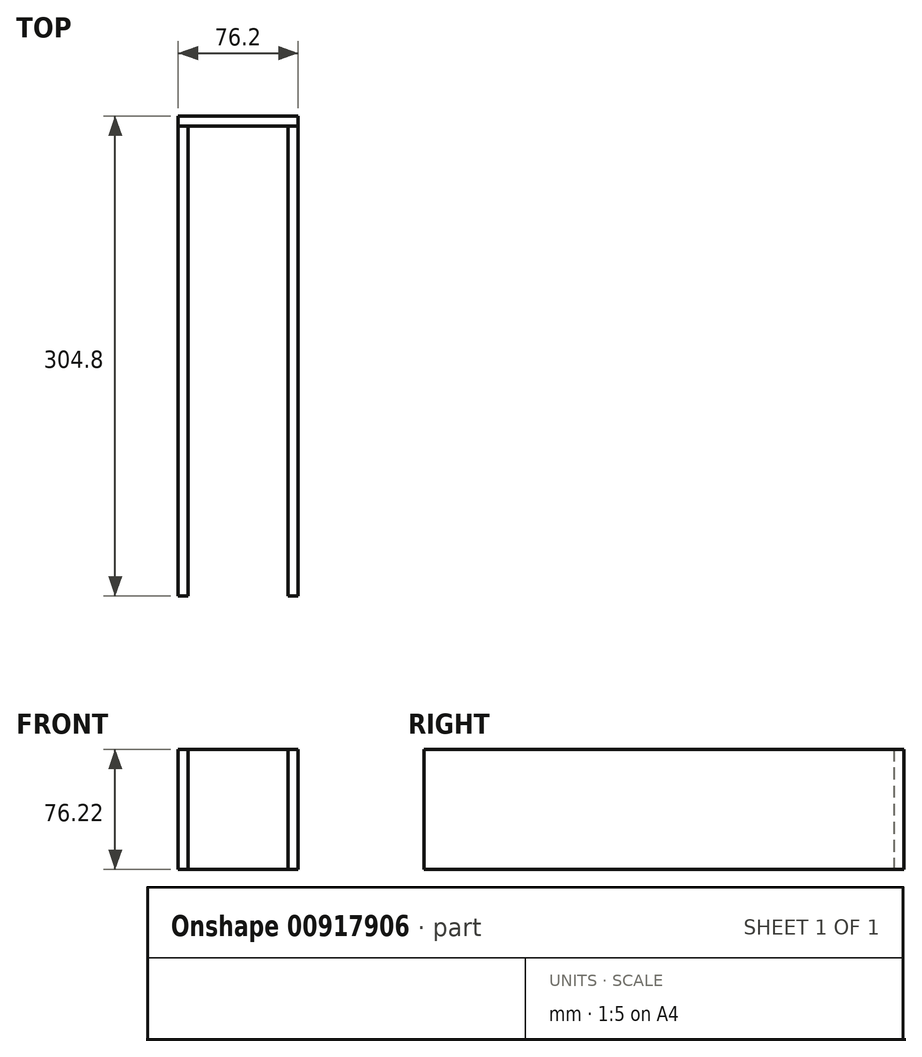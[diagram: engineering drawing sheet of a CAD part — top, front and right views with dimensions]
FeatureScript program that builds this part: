
annotation { "Feature Type Name" : "Feature", "Feature Type Description" : "" }
export const myFeature = defineFeature(function(context is Context, id is Id, definition is map)
    precondition{}
    {
        {
            var Q0;
            Q0=qCreatedBy(makeId("Right.planeOp"),FACE);
            var sketch = newSketch(context, id + "F0", { "sketchPlane" : qUnion([Q0])});
            skLineSegment(sketch, "E0", {"start": v(0, 0) * mm, "end": v(304.8, 0) * mm});
            skLineSegment(sketch, "E1", {"start": v(304.8, 0) * mm, "end": v(304.8, 76.2) * mm});
            skLineSegment(sketch, "E2", {"start": v(304.8, 76.2) * mm, "end": v(0, 76.2) * mm});
            skLineSegment(sketch, "E3", {"start": v(0, 76.2) * mm, "end": v(0, 0) * mm});
            skSolve(sketch);
        }
        {
            var Q0;
            Q0 = qSketchRegion(id + "F0", true);
            extrude(context, id + "F1", {"entities" : qUnion([Q0]), "depth" : 6.35 * mm, "offsetDistance" : 25 * mm});
        }
        {
            var Q0;
            Q0=qCreatedBy(makeId("Right.planeOp"),FACE);
            var sketch = newSketch(context, id + "F2", { "sketchPlane" : qUnion([Q0])});
            skLineSegment(sketch, "E4", {"start": v(304.8, 76.2) * mm, "end": v(304.8, 0) * mm});
            skLineSegment(sketch, "E5", {"start": v(304.8, 0) * mm, "end": v(298.47, 0) * mm});
            skLineSegment(sketch, "E6", {"start": v(298.47, 0) * mm, "end": v(298.47, 76.22) * mm});
            skLineSegment(sketch, "E7", {"start": v(298.47, 76.22) * mm, "end": v(304.8, 76.2) * mm});
            skSolve(sketch);
        }
        {
            var Q0;
            Q0 = qSketchRegion(id + "F2", true);
            extrude(context, id + "F3", {"entities" : qUnion([Q0]), "operationType" : NewBodyOperationType.ADD, "depth" : 76.2 * mm, "offsetDistance" : 25 * mm});
        }
        {
            var Q0;
            Q0=makeQuery(id+"F3.opExtrude","CAP_FACE",FACE,{"disambiguationData":[OSD([sQuery(id+"F2.wireOp",EDGE,"E4"),sQuery(id+"F2.wireOp",EDGE,"E5"),sQuery(id+"F2.wireOp",EDGE,"E6"),sQuery(id+"F2.wireOp",EDGE,"E7")])],"isStart":false});
            cPlane(context, id + "F4", {"entities" : qUnion([Q0]), "cplaneType" : CPlaneType.OFFSET, "offset" : 0 * mm, "oppositeDirection" : true, "width" : 150 * mm, "height" : 150 * mm});
        }
        {
            var Q0;
            Q0=qCreatedBy(id+"F4.planeOp",FACE);
            var sketch = newSketch(context, id + "F5", { "sketchPlane" : qUnion([Q0])});
            skLineSegment(sketch, "E8.bottom", {"start": v(304.8, 0) * mm, "end": v(0, 0) * mm});
            skLineSegment(sketch, "E8.top", {"start": v(304.8, 76.2) * mm, "end": v(0, 76.2) * mm});
            skLineSegment(sketch, "E8.left", {"start": v(304.8, 0) * mm, "end": v(304.8, 76.2) * mm});
            skLineSegment(sketch, "E8.right", {"start": v(0, 0) * mm, "end": v(0, 76.2) * mm});
            skSolve(sketch);
        }
        {
            var Q0;
            Q0 = qSketchRegion(id + "F5", true);
            extrude(context, id + "F6", {"entities" : qUnion([Q0]), "operationType" : NewBodyOperationType.ADD, "oppositeDirection" : true, "depth" : 6.35 * mm, "offsetDistance" : 25 * mm});
        }
    });
